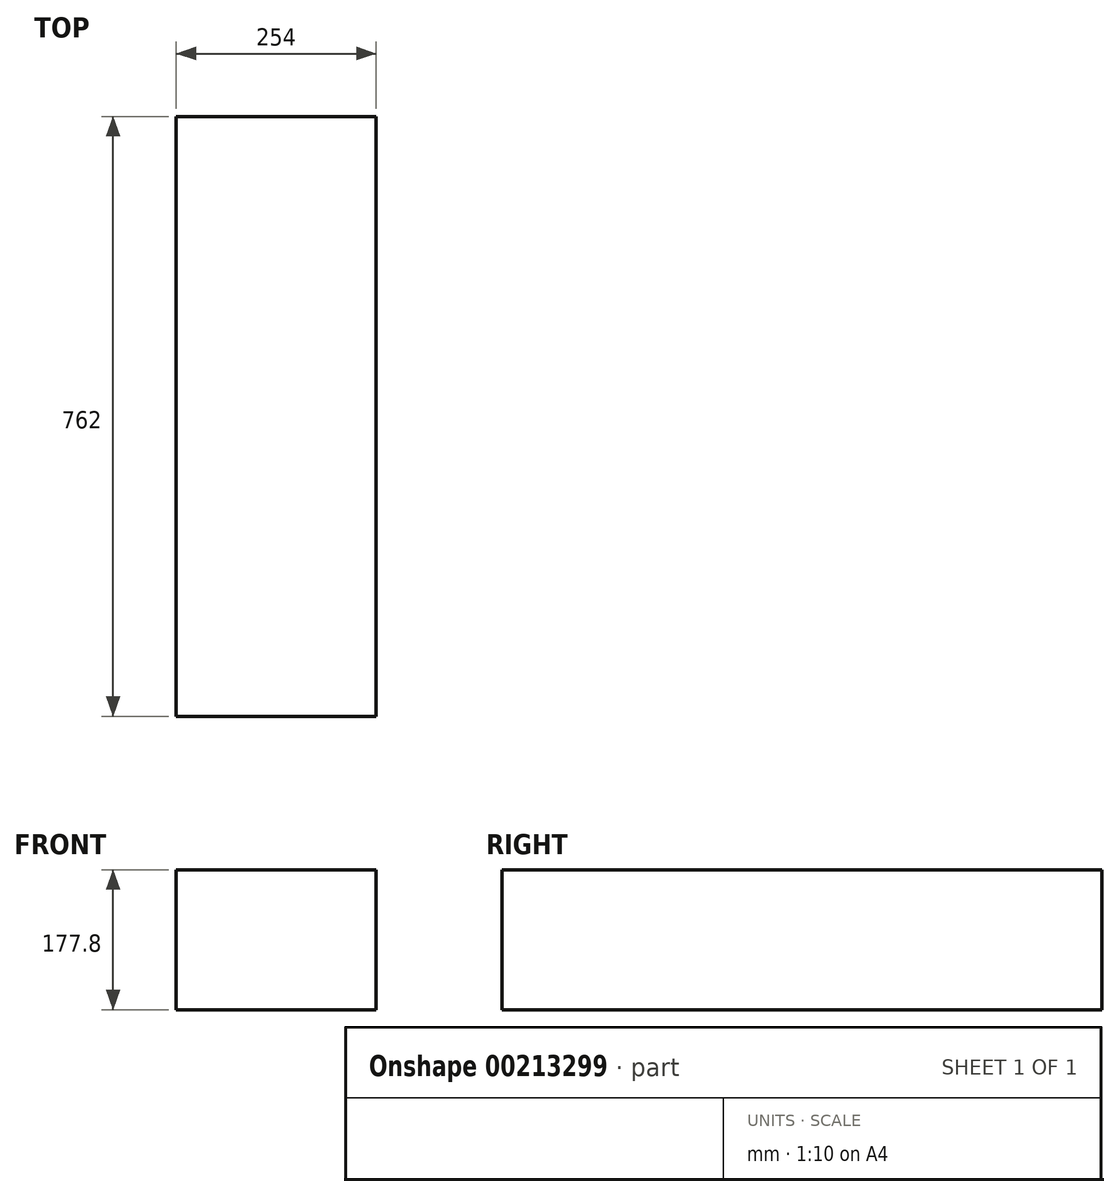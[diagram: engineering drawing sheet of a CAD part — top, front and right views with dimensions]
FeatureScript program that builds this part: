
annotation { "Feature Type Name" : "Feature", "Feature Type Description" : "" }
export const myFeature = defineFeature(function(context is Context, id is Id, definition is map)
    precondition{}
    {
        {
            var Q0;
            Q0=qCreatedBy(makeId("Front.planeOp"),FACE);
            var sketch = newSketch(context, id + "F3", { "sketchPlane" : qUnion([Q0])});
            skLineSegment(sketch, "E0.bottom", {"start": v(0, 0) * mm, "end": v(-254, 0) * mm});
            skLineSegment(sketch, "E0.top", {"start": v(0, 177.8) * mm, "end": v(-254, 177.8) * mm});
            skLineSegment(sketch, "E0.left", {"start": v(0, 0) * mm, "end": v(0, 177.8) * mm});
            skLineSegment(sketch, "E0.right", {"start": v(-254, 0) * mm, "end": v(-254, 177.8) * mm});
            skSolve(sketch);
        }
        {
            var Q0;
            Q0=makeQuery(id+"F3.imprint","IMPRINT",FACE,{"disambiguationData":[TD([[makeQuery(id+"F3.imprint","IMPRINT",EDGE,{"derivedFrom":sQuery(id+"F3.wireOp",EDGE,"E0.bottom")}),-1.0]])]});
            extrude(context, id + "F0", {"entities" : qUnion([Q0]), "depth" : 762 * mm});
        }
    });
